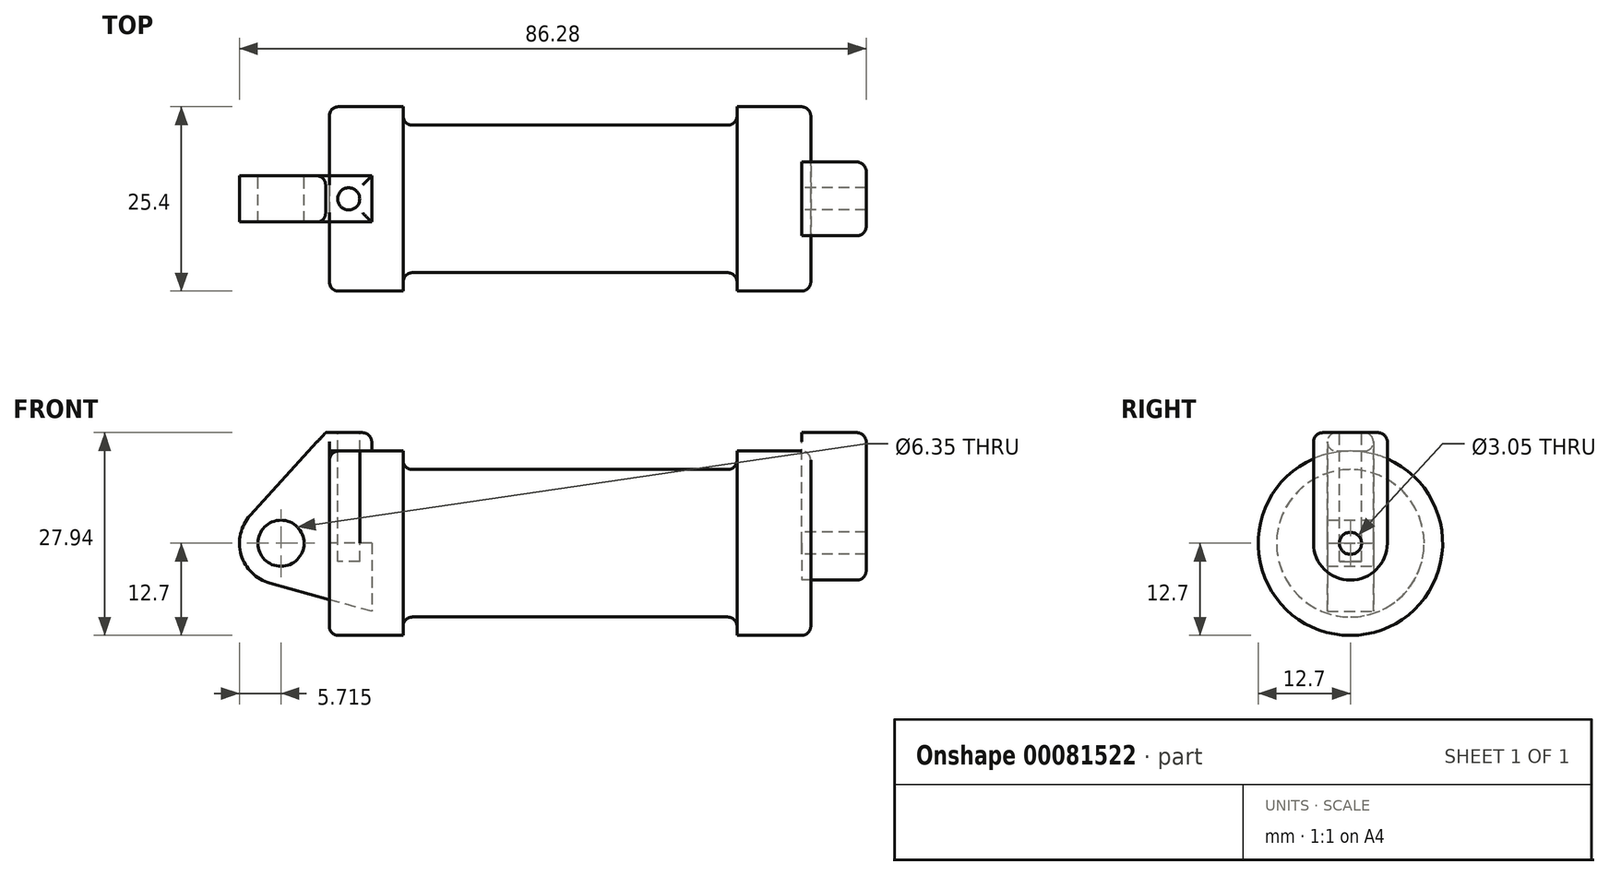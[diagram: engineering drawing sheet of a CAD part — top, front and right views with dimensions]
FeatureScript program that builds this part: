
annotation { "Feature Type Name" : "Feature", "Feature Type Description" : "" }
export const myFeature = defineFeature(function(context is Context, id is Id, definition is map)
    precondition{}
    {
        {
            var Q0;
            Q0=qCreatedBy(makeId("Front.planeOp"),FACE);
            var sketch = newSketch(context, id + "F0", { "sketchPlane" : qUnion([Q0])});
            skLineSegment(sketch, "E0", {"start": v(0, 0) * mm, "end": v(0, 12.7) * mm});
            skLineSegment(sketch, "E1", {"start": v(0, 12.7) * mm, "end": v(10.16, 12.7) * mm});
            skLineSegment(sketch, "E2", {"start": v(10.16, 12.7) * mm, "end": v(10.16, 10.16) * mm});
            skLineSegment(sketch, "E3", {"start": v(10.16, 10.16) * mm, "end": v(56.13, 10.16) * mm});
            skLineSegment(sketch, "E4", {"start": v(56.13, 10.16) * mm, "end": v(56.13, 12.7) * mm});
            skLineSegment(sketch, "E5", {"start": v(56.13, 12.7) * mm, "end": v(66.3, 12.7) * mm});
            skLineSegment(sketch, "E6", {"start": v(66.3, 12.7) * mm, "end": v(66.3, 0) * mm});
            skLineSegment(sketch, "E7", {"start": v(66.3, 0) * mm, "end": v(0, 0) * mm});
            skLineSegment(sketch, "E8", {"start": v(5.84, 15.24) * mm, "end": v(-0.5, 15.24) * mm});
            skLineSegment(sketch, "E9", {"start": v(-0.5, 15.24) * mm, "end": v(-10.88, 3.85) * mm});
            skLineSegment(sketch, "E10", {"start": v(0, 0) * mm, "end": v(-6.65, 0) * mm});
            skCircle(sketch, "E11", {"center": v(-6.65, 0) * mm, "radius": 5.72 * mm});
            skCircle(sketch, "E12", {"center": v(-6.65, 0) * mm, "radius": 3.18 * mm});
            skLineSegment(sketch, "E13", {"start": v(5.84, 15.24) * mm, "end": v(5.84, -9.4) * mm});
            skLineSegment(sketch, "E14", {"start": v(5.84, -9.4) * mm, "end": v(-8.18, -5.5) * mm});
            skSolve(sketch);
        }
        {
            var Q0;
            {var subQ0=sQuery(id+"F0.wireOp",EDGE,"E2");Q0=makeQuery(id+"F0.imprint","IMPRINT",FACE,{"disambiguationData":[TD([[makeQuery(id+"F0.imprint","IMPRINT",EDGE,{"derivedFrom":subQ0}),-1.0]])]});}
            var Q1;
            {var subQ0=sQuery(id+"F0.wireOp",EDGE,"E0");Q1=makeQuery(id+"F0.imprint","IMPRINT",FACE,{"disambiguationData":[TD([[makeQuery(id+"F0.imprint","IMPRINT",EDGE,{"derivedFrom":subQ0}),-1.0]])]});}
            var Q2;
            Q2=sQuery(id+"F0.wireOp",EDGE,"E7");
            revolve(context, id + "F1", {"entities" : qUnion([Q0, Q1]), "axis" : qUnion([Q2]), "revolveType" : RevolveType.FULL});
        }
        {
            var Q0;
            {var subQ3=sQuery(id+"F0.wireOp",EDGE,"E0");Q0=makeQuery(id+"F0.imprint","IMPRINT",FACE,{"disambiguationData":[TD([[makeQuery(id+"F0.imprint","IMPRINT",EDGE,{"derivedFrom":subQ3}),1.0]])]});}
            var Q1;
            {var subQ4=sQuery(id+"F0.wireOp",EDGE,"E12");Q1=makeQuery(id+"F0.imprint","IMPRINT",FACE,{"disambiguationData":[TD([[makeQuery(id+"F0.imprint","IMPRINT",EDGE,{"derivedFrom":subQ4}),-1.0]])]});}
            var Q2;
            {var subQ0=sQuery(id+"F0.wireOp",EDGE,"E14");Q2=makeQuery(id+"F0.imprint","IMPRINT",FACE,{"disambiguationData":[TD([[makeQuery(id+"F0.imprint","IMPRINT",EDGE,{"derivedFrom":subQ0}),-1.0]])]});}
            extrude(context, id + "F2", {"entities" : qUnion([Q0, Q1, Q2]), "endBound" : BoundingType.SYMMETRIC, "depth" : 6.35 * mm});
        }
        {
            var Q0;
            Q0=makeQuery(id+"F1.opRevolve","SWEPT_FACE",FACE,{"disambiguationData":[OSD([sQuery(id+"F0.wireOp",EDGE,"E6")])]});
            var sketch = newSketch(context, id + "F3", { "sketchPlane" : qUnion([Q0])});
            skCircle(sketch, "E15", {"center": v(0, 0) * mm, "radius": 1.52 * mm});
            skCircle(sketch, "E16", {"center": v(0, 0) * mm, "radius": 5.08 * mm});
            skLineSegment(sketch, "E17", {"start": v(-5.08, 0) * mm, "end": v(-5.08, 15.24) * mm});
            skLineSegment(sketch, "E18", {"start": v(5.08, 0) * mm, "end": v(5.08, 15.24) * mm});
            skLineSegment(sketch, "E19", {"start": v(-5.08, 15.24) * mm, "end": v(5.08, 15.24) * mm});
            skSolve(sketch);
        }
        {
            var Q0;
            Q0 = qSketchRegion(id + "F3", true);
            extrude(context, id + "F4", {"entities" : qUnion([Q0]), "depth" : 7.62 * mm, "hasSecondDirection" : true, "secondDirectionOppositeDirection" : true, "secondDirectionDepth" : 1.27 * mm});
        }
        {
            var Q0;
            Q0=makeQuery(id+"F4.opExtrude","SWEPT_FACE",FACE,{"disambiguationData":[OSD([sQuery(id+"F3.wireOp",EDGE,"E19")])]});
            var sketch = newSketch(context, id + "F5", { "sketchPlane" : qUnion([Q0])});
            skCircle(sketch, "E20", {"center": v(69.47, 0) * mm, "radius": 1.52 * mm});
            skSolve(sketch);
        }
        {
            var Q0;
            Q0=sQuery(id+"F5.wireOp",EDGE,"E20");
            extrude(context, id + "F6", {"bodyType" : ToolBodyType.SURFACE, "surfaceEntities" : qUnion([Q0]), "oppositeDirection" : true, "depth" : 10.4 * mm});
        }
        {
            var Q0;
            Q0=makeQuery(id+"F2.opExtrude","SWEPT_FACE",FACE,{"disambiguationData":[OSD([sQuery(id+"F0.wireOp",EDGE,"E8")])]});
            var sketch = newSketch(context, id + "F7", { "sketchPlane" : qUnion([Q0])});
            skCircle(sketch, "E21", {"center": v(2.67, 0) * mm, "radius": 1.52 * mm});
            skSolve(sketch);
        }
        {
            var Q0;
            Q0 = qSketchRegion(id + "F7", true);
            extrude(context, id + "F8", {"entities" : qUnion([Q0]), "oppositeDirection" : true, "depth" : 17.78 * mm});
        }
        {
            var Q0;
            Q0=makeQuery(id+"F1.opRevolve","SWEPT_EDGE",EDGE,{"disambiguationData":[OSD([sQuery(id+"F0.wireOp",EDGE,"E2"),sQuery(id+"F0.wireOp",EDGE,"E3")])]});
            fillet(context, id + "F9", {"entities" : qUnion([Q0]), "radius" : 1.27 * mm, "allowEdgeOverflow" : false});
        }
        {
            var Q0;
            Q0=makeQuery(id+"F1.opRevolve","SWEPT_EDGE",EDGE,{"disambiguationData":[OSD([sQuery(id+"F0.wireOp",EDGE,"E3"),sQuery(id+"F0.wireOp",EDGE,"E4")])]});
            fillet(context, id + "F10", {"entities" : qUnion([Q0]), "radius" : 1.27 * mm, "tangentPropagation" : true, "allowEdgeOverflow" : false});
        }
        {
            var Q0;
            Q0=makeQuery(id+"F4.opExtrude","SWEPT_EDGE",EDGE,{"disambiguationData":[OSD([sQuery(id+"F3.wireOp",EDGE,"E17"),sQuery(id+"F3.wireOp",EDGE,"E19")])]});
            fillet(context, id + "F11", {"entities" : qUnion([Q0]), "radius" : 1.27 * mm, "tangentPropagation" : true, "allowEdgeOverflow" : false});
        }
        {
            var Q0;
            Q0=makeQuery(id+"F4.opExtrude","CAP_EDGE",EDGE,{"disambiguationData":[OSD([sQuery(id+"F3.wireOp",EDGE,"E19")])],"isStart":false});
            var Q1;
            Q1=makeQuery(id+"F4.opExtrude","SWEPT_EDGE",EDGE,{"disambiguationData":[OSD([sQuery(id+"F3.wireOp",EDGE,"E18"),sQuery(id+"F3.wireOp",EDGE,"E19")])]});
            var Q2;
            Q2=makeQuery(id+"F1.opRevolve","SWEPT_EDGE",EDGE,{"disambiguationData":[OSD([sQuery(id+"F0.wireOp",EDGE,"E5"),sQuery(id+"F0.wireOp",EDGE,"E6")])]});
            var Q3;
            Q3=makeQuery(id+"F2.opExtrude","CAP_EDGE",EDGE,{"disambiguationData":[OSD([sQuery(id+"F0.wireOp",EDGE,"E8")])],"isStart":false});
            var Q4;
            Q4=makeQuery(id+"F2.opExtrude","CAP_EDGE",EDGE,{"disambiguationData":[OSD([sQuery(id+"F0.wireOp",EDGE,"E1")])],"isStart":false});
            var Q5;
            Q5=makeQuery(id+"F2.opExtrude","CAP_EDGE",EDGE,{"disambiguationData":[OSD([sQuery(id+"F0.wireOp",EDGE,"E8")])],"isStart":true});
            var Q6;
            Q6=makeQuery(id+"F2.opExtrude","CAP_EDGE",EDGE,{"disambiguationData":[OSD([sQuery(id+"F0.wireOp",EDGE,"E1")])],"isStart":true});
            var Q7;
            Q7=makeQuery(id+"F2.opExtrude","SWEPT_EDGE",EDGE,{"disambiguationData":[OSD([sQuery(id+"F0.wireOp",EDGE,"E8"),sQuery(id+"F0.wireOp",EDGE,"E13")])]});
            fillet(context, id + "F12", {"entities" : qUnion([Q0, Q1, Q2, Q3, Q4, Q5, Q6, Q7]), "radius" : 1.27 * mm, "tangentPropagation" : true, "allowEdgeOverflow" : false});
        }
        {
            var Q0;
            Q0=makeQuery(id+"F1.opRevolve","SWEPT_EDGE",EDGE,{"disambiguationData":[OSD([sQuery(id+"F0.wireOp",EDGE,"E0"),sQuery(id+"F0.wireOp",EDGE,"E1")])]});
            fillet(context, id + "F13", {"entities" : qUnion([Q0]), "radius" : 1.27 * mm, "tangentPropagation" : true, "allowEdgeOverflow" : false});
        }
    });
